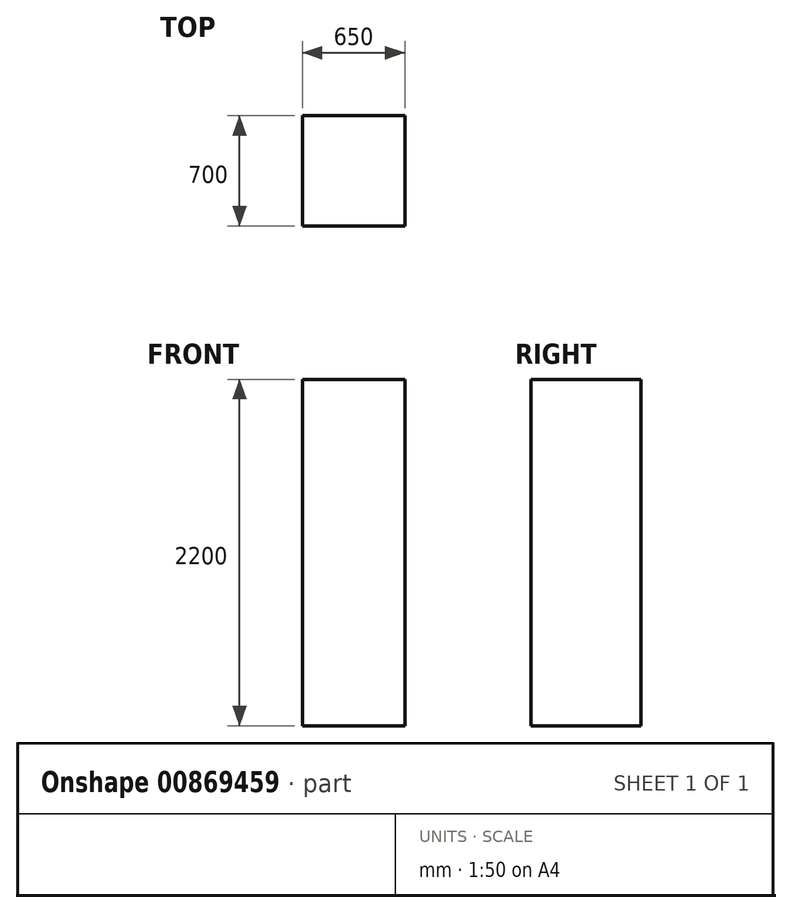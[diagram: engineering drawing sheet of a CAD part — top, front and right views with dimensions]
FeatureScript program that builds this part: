
annotation { "Feature Type Name" : "Feature", "Feature Type Description" : "" }
export const myFeature = defineFeature(function(context is Context, id is Id, definition is map)
    precondition{}
    {
        {
            var Q0;
            Q0=qCreatedBy(makeId("Top.planeOp"),FACE);
            var sketch = newSketch(context, id + "F0", { "sketchPlane" : qUnion([Q0])});
            skLineSegment(sketch, "E0.bottom", {"start": v(0, 0) * mm, "end": v(650, 0) * mm});
            skLineSegment(sketch, "E0.top", {"start": v(0, 700) * mm, "end": v(650, 700) * mm});
            skLineSegment(sketch, "E0.left", {"start": v(0, 0) * mm, "end": v(0, 700) * mm});
            skLineSegment(sketch, "E0.right", {"start": v(650, 0) * mm, "end": v(650, 700) * mm});
            skSolve(sketch);
        }
        {
            var Q0;
            Q0=makeQuery(id+"F0.imprint","IMPRINT",FACE,{"disambiguationData":[TD([[makeQuery(id+"F0.imprint","IMPRINT",EDGE,{"derivedFrom":sQuery(id+"F0.wireOp",EDGE,"E0.bottom")}),1.0]])]});
            extrude(context, id + "F1", {"entities" : qUnion([Q0]), "depth" : 2200 * mm, "offsetDistance" : 25 * mm});
        }
    });
